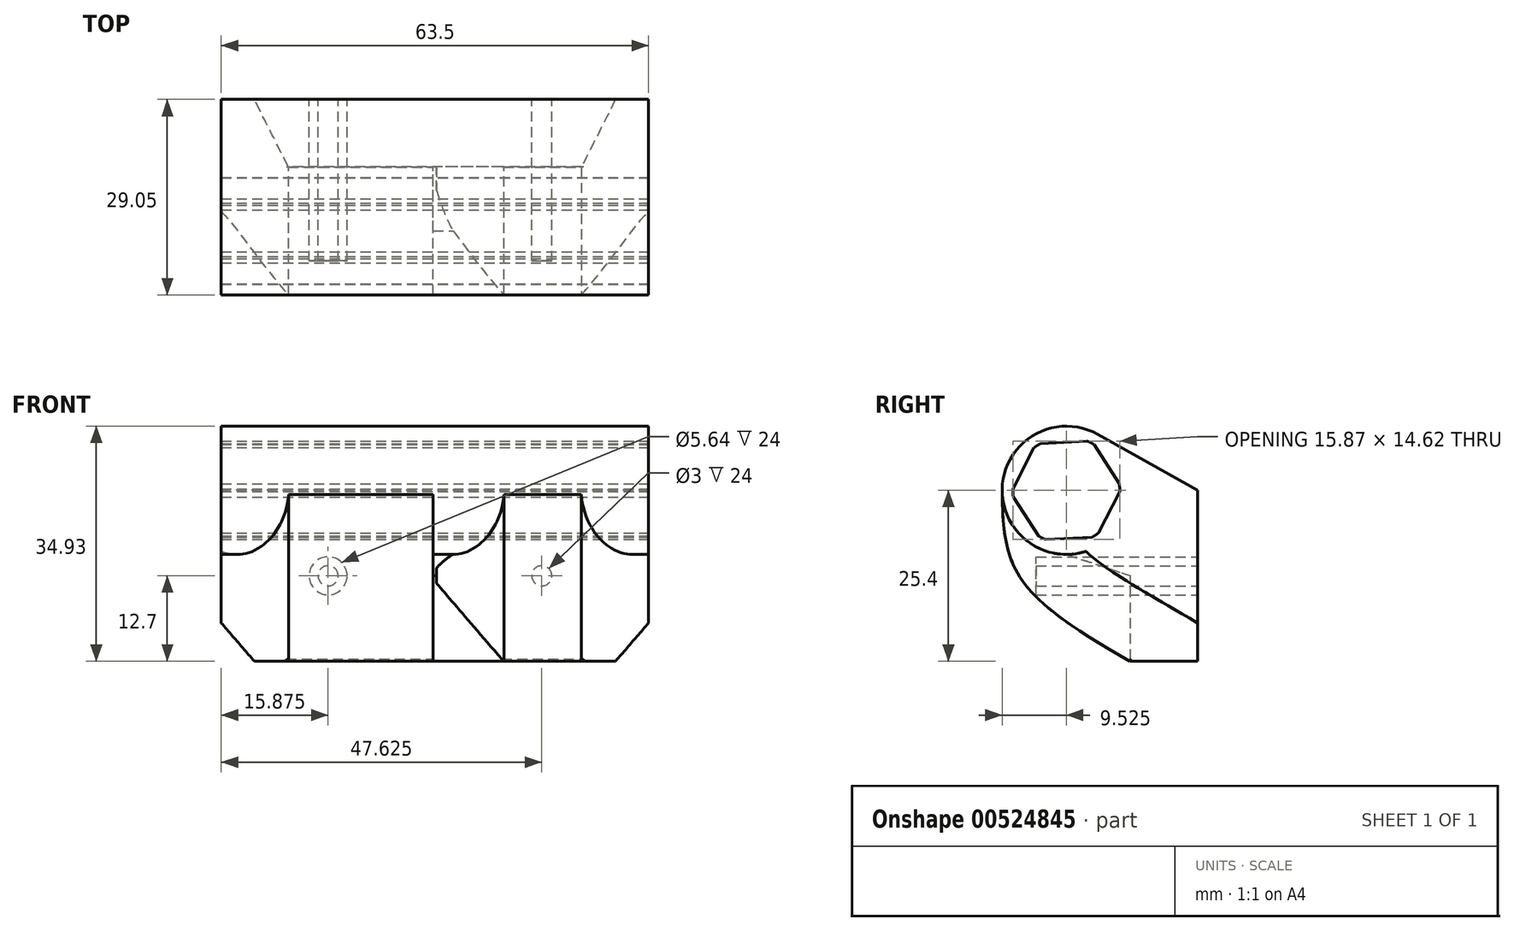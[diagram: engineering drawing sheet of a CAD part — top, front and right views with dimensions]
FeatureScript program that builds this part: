
annotation { "Feature Type Name" : "Feature", "Feature Type Description" : "" }
export const myFeature = defineFeature(function(context is Context, id is Id, definition is map)
    precondition{}
    {
        {
            var Q0;
            Q0=qCreatedBy(makeId("Front.planeOp"),FACE);
            var sketch = newSketch(context, id + "F0", { "sketchPlane" : qUnion([Q0])});
            skLineSegment(sketch, "E0.bottom", {"start": v(31.75, 0) * mm, "end": v(-31.75, 0) * mm});
            skLineSegment(sketch, "E0.top", {"start": v(31.75, 25.4) * mm, "end": v(-31.75, 25.4) * mm});
            skLineSegment(sketch, "E0.left", {"start": v(31.75, 0) * mm, "end": v(31.75, 25.4) * mm});
            skLineSegment(sketch, "E0.right", {"start": v(-31.75, 0) * mm, "end": v(-31.75, 25.4) * mm});
            skLineSegment(sketch, "E1", {"start": v(-31.75, 18.35) * mm, "end": v(0, 18.35) * mm, "construction": true});
            skLineSegment(sketch, "E2", {"start": v(0, 21.33) * mm, "end": v(31.75, 21.33) * mm, "construction": true});
            skCircle(sketch, "E3", {"center": v(15.87, 12.7) * mm, "radius": 2.82 * mm});
            skLineSegment(sketch, "E4", {"start": v(15.88, 12.7) * mm, "end": v(15.88, 25.4) * mm, "construction": true});
            skLineSegment(sketch, "E5", {"start": v(15.88, 12.7) * mm, "end": v(15.88, 0) * mm, "construction": true});
            skCircle(sketch, "E6.MirrorC", {"center": v(-15.87, 12.7) * mm, "radius": 2.82 * mm});
            skSolve(sketch);
        }
        {
            var Q0;
            Q0 = qSketchRegion(id + "F0", true);
            extrude(context, id + "F1", {"entities" : qUnion([Q0]), "depth" : 10 * mm, "offsetDistance" : 25 * mm});
        }
        {
            var Q0;
            Q0=makeQuery(id+"F1.opExtrude","SWEPT_FACE",FACE,{"disambiguationData":[OSD([sQuery(id+"F0.wireOp",EDGE,"E0.left")])]});
            var sketch = newSketch(context, id + "F2", { "sketchPlane" : qUnion([Q0])});
            skLineSegment(sketch, "E7", {"start": v(-10, 25.4) * mm, "end": v(-34.12, 25.4) * mm, "construction": true});
            skCircle(sketch, "E8", {"center": v(-19.53, 25.4) * mm, "radius": 9.53 * mm});
            skLineSegment(sketch, "E9", {"start": v(-19.53, 15.87) * mm, "end": v(-10, 12.7) * mm});
            skCircle(sketch, "E10", {"center": v(-19.53, 25.4) * mm, "radius": 7.94 * mm});
            skSolve(sketch);
        }
        {
            var Q0;
            {var subQ4=sQuery(id+"F2.wireOp",EDGE,"E9");Q0=makeQuery(id+"F2.imprint","IMPRINT",FACE,{"disambiguationData":[TD([[makeQuery(id+"F2.imprint","IMPRINT",EDGE,{"derivedFrom":subQ4}),1.0]])]});}
            var Q1;
            Q1=makeQuery(id+"F2.imprint","IMPRINT",FACE,{"disambiguationData":[TD([[makeQuery(id+"F2.imprint","IMPRINT",EDGE,{"derivedFrom":sQuery(id+"F2.wireOp",EDGE,"E10")}),-1.0]])]});
            extrude(context, id + "F3", {"entities" : qUnion([Q0, Q1]), "operationType" : NewBodyOperationType.ADD, "oppositeDirection" : true, "depth" : 63.5 * mm, "offsetDistance" : 25 * mm});
        }
        {
            var Q0;
            {var subQ0=sQuery(id+"F0.wireOp",EDGE,"E0.left");Q0=makeQuery(id+"F3.boolean.opBoolean","MERGE",FACE,{"derivedFrom":[makeQuery(id+"F1.opExtrude","SWEPT_FACE",FACE,{"disambiguationData":[OSD([subQ0])]}),makeQuery(id+"F3.opExtrude","CAP_FACE",FACE,{"disambiguationData":[OSD([subQ0,sQuery(id+"F2.wireOp",EDGE,"E8"),sQuery(id+"F2.wireOp",EDGE,"E9"),sQuery(id+"F2.wireOp",EDGE,"E10")])],"isStart":true})]});}
            var sketch = newSketch(context, id + "F4", { "sketchPlane" : qUnion([Q0])});
            skLineSegment(sketch, "E11", {"start": v(0, 12.7) * mm, "end": v(-20, 12.7) * mm, "construction": true});
            skSolve(sketch);
        }
        {
            var Q0;
            {var subQ0=sQuery(id+"F0.wireOp",EDGE,"E0.left");Q0=makeQuery(id+"F4.imprint","IMPRINT",FACE,{"disambiguationData":[TD([[makeQuery(id+"F4.imprint","IMPRINT",EDGE,{"derivedFrom":makeQuery(id+"F1.opExtrude","CAP_EDGE",EDGE,{"disambiguationData":[OSD([subQ0])],"isStart":true})}),1.0]])]});}
            var sketch = newSketch(context, id + "F5", { "sketchPlane" : qUnion([Q0])});
            skFitSpline(sketch, "E12", {"points": [v(-29.03, 25.89) * mm, v(-26.61, 12.82) * mm, v(-10.1, 0) * mm], "startDerivative": vector(0.09, -30.89) * mm, "endDerivative": vector(36.43, -21.25) * mm});
            skLineSegment(sketch, "E13", {"start": v(-29.03, 25.89) * mm, "end": v(-27.55, 22.17) * mm});
            skLineSegment(sketch, "E14", {"start": v(-27.55, 22.17) * mm, "end": v(-27.12, 20.26) * mm});
            skLineSegment(sketch, "E15", {"start": v(-27.12, 20.26) * mm, "end": v(-22.24, 17.11) * mm});
            skLineSegment(sketch, "E16", {"start": v(-22.24, 17.11) * mm, "end": v(-14.9, 15.88) * mm});
            skLineSegment(sketch, "E17", {"start": v(-14.9, 15.88) * mm, "end": v(-6.62, 13.4) * mm});
            skLineSegment(sketch, "E18", {"start": v(-6.62, 13.4) * mm, "end": v(-7.8, 7.91) * mm});
            skLineSegment(sketch, "E19", {"start": v(-7.8, 7.91) * mm, "end": v(-10.1, 0) * mm});
            skSolve(sketch);
        }
        {
            var Q0;
            {var subQ0=makeQuery(id+"F4.imprint","IMPRINT",EDGE,{"derivedFrom":makeQuery(id+"F3.opExtrude","CAP_EDGE",EDGE,{"disambiguationData":[OSD([sQuery(id+"F2.wireOp",EDGE,"E9")])],"isStart":true})});Q0=makeQuery(id+"F5.imprint","IMPRINT",FACE,{"disambiguationData":[TD([[makeQuery(id+"F5.imprint","IMPRINT",EDGE,{"derivedFrom":subQ0}),-1.0]])]});}
            extrude(context, id + "F6", {"entities" : qUnion([Q0]), "operationType" : NewBodyOperationType.ADD, "oppositeDirection" : true, "depth" : 63.5 * mm, "offsetDistance" : 25 * mm});
        }
        {
            var Q0;
            Q0=makeQuery(id+"F1.opExtrude","CAP_FACE",FACE,{"disambiguationData":[OSD([sQuery(id+"F0.wireOp",EDGE,"E0.bottom"),sQuery(id+"F0.wireOp",EDGE,"E0.top"),sQuery(id+"F0.wireOp",EDGE,"E0.left"),sQuery(id+"F0.wireOp",EDGE,"E0.right"),sQuery(id+"F0.wireOp",EDGE,"E3"),sQuery(id+"F0.wireOp",EDGE,"E6.MirrorC")])],"isStart":true});
            var sketch = newSketch(context, id + "F7", { "sketchPlane" : qUnion([Q0])});
            skCircle(sketch, "E20", {"center": v(-15.87, 12.7) * mm, "radius": 1.5 * mm});
            skCircle(sketch, "E21.MirrorC", {"center": v(15.87, 12.7) * mm, "radius": 1.5 * mm});
            skSolve(sketch);
        }
        {
            var Q0;
            Q0=makeQuery(id+"F7.imprint","IMPRINT",FACE,{"disambiguationData":[TD([[makeQuery(id+"F7.imprint","IMPRINT",EDGE,{"derivedFrom":sQuery(id+"F7.wireOp",EDGE,"E20")}),-1.0]])]});
            var Q1;
            Q1=makeQuery(id+"F7.imprint","IMPRINT",FACE,{"disambiguationData":[TD([[makeQuery(id+"F7.imprint","IMPRINT",EDGE,{"derivedFrom":sQuery(id+"F7.wireOp",EDGE,"E21.MirrorC")}),1.0]])]});
            extrude(context, id + "F8", {"entities" : qUnion([Q0, Q1]), "operationType" : NewBodyOperationType.ADD, "oppositeDirection" : true, "depth" : 20.1 * mm, "offsetDistance" : 25 * mm});
        }
        {
            var Q0;
            Q0=makeQuery(id+"F7.imprint","IMPRINT",FACE,{"disambiguationData":[TD([[makeQuery(id+"F7.imprint","IMPRINT",EDGE,{"derivedFrom":sQuery(id+"F7.wireOp",EDGE,"E21.MirrorC")}),-1.0]])]});
            var Q1;
            Q1=makeQuery(id+"F7.imprint","IMPRINT",FACE,{"disambiguationData":[TD([[makeQuery(id+"F7.imprint","IMPRINT",EDGE,{"derivedFrom":sQuery(id+"F7.wireOp",EDGE,"E20")}),1.0]])]});
            extrude(context, id + "F9", {"entities" : qUnion([Q0, Q1]), "operationType" : NewBodyOperationType.REMOVE, "oppositeDirection" : true, "depth" : 24 * mm, "offsetDistance" : 25 * mm});
        }
        {
            var Q0;
            {var subQ0=makeQuery(id+"F4.imprint","IMPRINT",EDGE,{"derivedFrom":makeQuery(id+"F3.opExtrude","CAP_EDGE",EDGE,{"disambiguationData":[OSD([sQuery(id+"F2.wireOp",EDGE,"E9")])],"isStart":true})});Q0=makeQuery(id+"F5.imprint","IMPRINT",FACE,{"disambiguationData":[TD([[makeQuery(id+"F5.imprint","IMPRINT",EDGE,{"derivedFrom":subQ0}),-1.0]])]});}
            extrude(context, id + "F10", {"entities" : qUnion([Q0]), "operationType" : NewBodyOperationType.REMOVE, "oppositeDirection" : true, "depth" : 32 * mm, "offsetDistance" : 25 * mm, "hasSecondDirection" : true, "secondDirectionOppositeDirection" : true, "secondDirectionDepth" : 31.5 * mm});
        }
        {
            var Q0;
            Q0=makeQuery(id+"F10.boolean.opBoolean","COPY",EDGE,{"derivedFrom":makeQuery(id+"F10.opExtrude","CAP_EDGE",EDGE,{"disambiguationData":[OSD([sQuery(id+"F5.wireOp",EDGE,"E12")])],"isStart":false})});
            var Q1;
            Q1=makeQuery(id+"F10.boolean.opBoolean","COPY",EDGE,{"derivedFrom":makeQuery(id+"F10.opExtrude","CAP_EDGE",EDGE,{"disambiguationData":[OSD([sQuery(id+"F5.wireOp",EDGE,"E12")])],"isStart":true})});
            var Q2;
            Q2=makeQuery(id+"F6.opExtrude","CAP_EDGE",EDGE,{"disambiguationData":[OSD([sQuery(id+"F5.wireOp",EDGE,"E12")])],"isStart":true});
            var Q3;
            Q3=makeQuery(id+"F6.opExtrude","CAP_EDGE",EDGE,{"disambiguationData":[OSD([sQuery(id+"F5.wireOp",EDGE,"E12")])],"isStart":false});
            chamfer(context, id + "F11", {"entities" : qUnion([Q0, Q1, Q2, Q3]), "width" : 10 * mm, "tangentPropagation" : true});
        }
        {
            var Q0;
            {var subQ0=sQuery(id+"F2.wireOp",EDGE,"E9");var subQ1=sQuery(id+"F2.wireOp",EDGE,"E8");var subQ2=sQuery(id+"F0.wireOp",EDGE,"E0.left");Q0=makeQuery(id+"F6.boolean.opBoolean","MERGE",FACE,{"derivedFrom":[makeQuery(id+"F3.boolean.opBoolean","MERGE",FACE,{"derivedFrom":[makeQuery(id+"F1.opExtrude","SWEPT_FACE",FACE,{"disambiguationData":[OSD([sQuery(id+"F0.wireOp",EDGE,"E0.right")])]}),makeQuery(id+"F3.opExtrude","CAP_FACE",FACE,{"disambiguationData":[OSD([subQ2,subQ1,subQ0,sQuery(id+"F2.wireOp",EDGE,"E10")])],"isStart":false})]}),makeQuery(id+"F6.opExtrude","CAP_FACE",FACE,{"disambiguationData":[OSD([subQ2,subQ1,subQ0,sQuery(id+"F5.wireOp",EDGE,"E12"),sQuery(id+"F5.wireOp",EDGE,"E19")])],"isStart":false})]});}
            var sketch = newSketch(context, id + "F12", { "sketchPlane" : qUnion([Q0])});
            skLineSegment(sketch, "E22", {"start": v(0, 25.4) * mm, "end": v(14.88, 33.71) * mm});
            skSolve(sketch);
        }
        {
            var Q0;
            {var subQ0=sQuery(id+"F12.wireOp",EDGE,"E22");Q0=makeQuery(id+"F12.imprint","IMPRINT",FACE,{"disambiguationData":[TD([[makeQuery(id+"F12.imprint","IMPRINT",EDGE,{"derivedFrom":subQ0}),-1.0]])]});}
            extrude(context, id + "F13", {"entities" : qUnion([Q0]), "operationType" : NewBodyOperationType.ADD, "oppositeDirection" : true, "depth" : 63.5 * mm, "offsetDistance" : 25 * mm});
        }
        {
            var Q0;
            Q0=makeQuery(id+"F4.imprint","IMPRINT",FACE,{"disambiguationData":[TD([[makeQuery(id+"F4.imprint","IMPRINT",EDGE,{"derivedFrom":makeQuery(id+"F3.opExtrude","CAP_EDGE",EDGE,{"disambiguationData":[OSD([sQuery(id+"F2.wireOp",EDGE,"E10")])],"isStart":true})}),1.0]])]});
            var sketch = newSketch(context, id + "F14", { "sketchPlane" : qUnion([Q0])});
            skCircle(sketch, "E23.cCircle", {"center": v(-19.53, 25.4) * mm, "radius": 7.14 * mm, "construction": true});
            skLineSegment(sketch, "E23.0", {"start": v(-15.77, 32.75) * mm, "end": v(-11.29, 25.82) * mm});
            skLineSegment(sketch, "E23.1", {"start": v(-11.29, 25.82) * mm, "end": v(-15.04, 18.48) * mm});
            skLineSegment(sketch, "E23.2", {"start": v(-15.04, 18.48) * mm, "end": v(-23.28, 18.05) * mm});
            skLineSegment(sketch, "E23.3", {"start": v(-23.28, 18.05) * mm, "end": v(-27.76, 24.98) * mm});
            skLineSegment(sketch, "E23.4", {"start": v(-27.76, 24.98) * mm, "end": v(-24, 32.32) * mm});
            skLineSegment(sketch, "E23.5", {"start": v(-24, 32.32) * mm, "end": v(-15.77, 32.75) * mm});
            skPoint(sketch, "E23.0.midPoint", {"position": v(-13.53, 29.28) * mm});
            skCircle(sketch, "E24", {"center": v(-19.53, 25.4) * mm, "radius": 7.94 * mm});
            skSolve(sketch);
        }
        {
            var Q0;
            {var subQ0=sQuery(id+"F14.wireOp",EDGE,"E24");var subQ1=sQuery(id+"F14.wireOp",EDGE,"E23.2");var subQ2=makeQuery(id+"F14.imprint","INTERSECT",VERTEX,{"disambiguationData":[OD(0.0)],"derivedFrom":[subQ1,subQ0]});Q0=makeQuery(id+"F14.imprint","IMPRINT",FACE,{"disambiguationData":[TD([[makeQuery(id+"F14.imprint","IMPRINT",EDGE,{"disambiguationData":[TD([[subQ2,-1.0]])],"derivedFrom":subQ1}),1.0]])]});}
            var Q1;
            {var subQ0=sQuery(id+"F14.wireOp",EDGE,"E24");var subQ1=sQuery(id+"F14.wireOp",EDGE,"E23.4");var subQ2=makeQuery(id+"F14.imprint","INTERSECT",VERTEX,{"disambiguationData":[OD(0.0)],"derivedFrom":[subQ1,subQ0]});Q1=makeQuery(id+"F14.imprint","IMPRINT",FACE,{"disambiguationData":[TD([[makeQuery(id+"F14.imprint","IMPRINT",EDGE,{"disambiguationData":[TD([[subQ2,-1.0]])],"derivedFrom":subQ1}),1.0]])]});}
            var Q2;
            {var subQ0=sQuery(id+"F14.wireOp",EDGE,"E24");var subQ1=sQuery(id+"F14.wireOp",EDGE,"E23.1");var subQ2=makeQuery(id+"F14.imprint","INTERSECT",VERTEX,{"disambiguationData":[OD(0.0)],"derivedFrom":[subQ1,subQ0]});Q2=makeQuery(id+"F14.imprint","IMPRINT",FACE,{"disambiguationData":[TD([[makeQuery(id+"F14.imprint","IMPRINT",EDGE,{"disambiguationData":[TD([[subQ2,-1.0]])],"derivedFrom":subQ1}),1.0]])]});}
            var Q3;
            {var subQ0=sQuery(id+"F14.wireOp",EDGE,"E24");var subQ1=sQuery(id+"F14.wireOp",EDGE,"E23.3");var subQ2=makeQuery(id+"F14.imprint","INTERSECT",VERTEX,{"disambiguationData":[OD(0.0)],"derivedFrom":[subQ1,subQ0]});Q3=makeQuery(id+"F14.imprint","IMPRINT",FACE,{"disambiguationData":[TD([[makeQuery(id+"F14.imprint","IMPRINT",EDGE,{"disambiguationData":[TD([[subQ2,-1.0]])],"derivedFrom":subQ1}),1.0]])]});}
            var Q4;
            {var subQ0=sQuery(id+"F14.wireOp",EDGE,"E24");var subQ1=sQuery(id+"F14.wireOp",EDGE,"E23.0");var subQ2=makeQuery(id+"F14.imprint","INTERSECT",VERTEX,{"disambiguationData":[OD(0.0)],"derivedFrom":[subQ1,subQ0]});Q4=makeQuery(id+"F14.imprint","IMPRINT",FACE,{"disambiguationData":[TD([[makeQuery(id+"F14.imprint","IMPRINT",EDGE,{"disambiguationData":[TD([[subQ2,-1.0]])],"derivedFrom":subQ1}),1.0]])]});}
            var Q5;
            {var subQ0=sQuery(id+"F14.wireOp",EDGE,"E24");var subQ1=sQuery(id+"F14.wireOp",EDGE,"E23.5");var subQ2=makeQuery(id+"F14.imprint","INTERSECT",VERTEX,{"disambiguationData":[OD(0.0)],"derivedFrom":[subQ1,subQ0]});Q5=makeQuery(id+"F14.imprint","IMPRINT",FACE,{"disambiguationData":[TD([[makeQuery(id+"F14.imprint","IMPRINT",EDGE,{"disambiguationData":[TD([[subQ2,-1.0]])],"derivedFrom":subQ1}),1.0]])]});}
            extrude(context, id + "F15", {"entities" : qUnion([Q0, Q1, Q2, Q3, Q4, Q5]), "operationType" : NewBodyOperationType.ADD, "oppositeDirection" : true, "depth" : 63.5 * mm, "offsetDistance" : 25 * mm});
        }
    });
